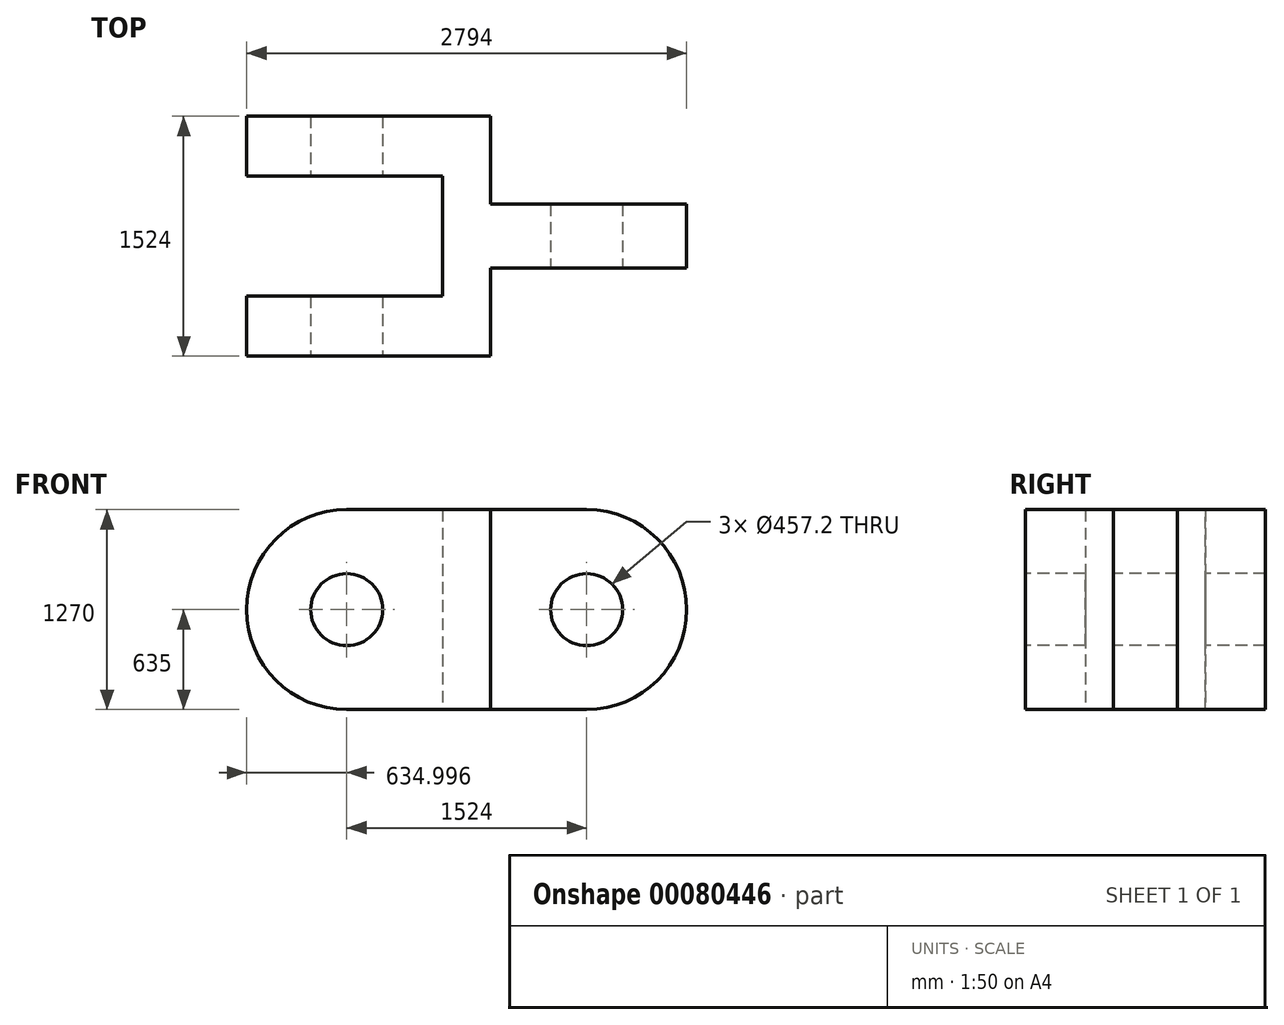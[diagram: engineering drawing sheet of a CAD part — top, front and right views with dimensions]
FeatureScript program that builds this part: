
annotation { "Feature Type Name" : "Feature", "Feature Type Description" : "" }
export const myFeature = defineFeature(function(context is Context, id is Id, definition is map)
    precondition{}
    {
        {
            var Q0;
            Q0=qCreatedBy(makeId("Top.planeOp"),FACE);
            var sketch = newSketch(context, id + "F0", { "sketchPlane" : qUnion([Q0])});
            skLineSegment(sketch, "E0", {"start": v(-848.91, 515.52) * mm, "end": v(-848.91, 134.52) * mm});
            skLineSegment(sketch, "E1", {"start": v(-848.91, 134.52) * mm, "end": v(395.69, 134.52) * mm});
            skLineSegment(sketch, "E2", {"start": v(395.69, 134.52) * mm, "end": v(395.69, -627.48) * mm});
            skLineSegment(sketch, "E3", {"start": v(395.69, -627.48) * mm, "end": v(-848.91, -627.48) * mm});
            skLineSegment(sketch, "E4", {"start": v(-848.91, -627.48) * mm, "end": v(-848.91, -1008.48) * mm});
            skLineSegment(sketch, "E5", {"start": v(-848.91, -1008.48) * mm, "end": v(700.49, -1008.48) * mm});
            skLineSegment(sketch, "E6", {"start": v(700.49, -1008.48) * mm, "end": v(700.49, -449.68) * mm});
            skLineSegment(sketch, "E7", {"start": v(700.49, -449.68) * mm, "end": v(1945.09, -449.68) * mm});
            skLineSegment(sketch, "E8", {"start": v(1945.09, -449.68) * mm, "end": v(1945.09, -43.28) * mm});
            skLineSegment(sketch, "E9", {"start": v(1945.09, -43.28) * mm, "end": v(700.49, -43.28) * mm});
            skLineSegment(sketch, "E10", {"start": v(700.49, -43.28) * mm, "end": v(700.49, 515.52) * mm});
            skLineSegment(sketch, "E11", {"start": v(700.49, 515.52) * mm, "end": v(-848.91, 515.52) * mm});
            skSolve(sketch);
        }
        {
            var Q0;
            Q0 = qSketchRegion(id + "F0", true);
            extrude(context, id + "F1", {"entities" : qUnion([Q0]), "depth" : 1270 * mm});
        }
        {
            var Q0;
            Q0=makeQuery(id+"F1.opExtrude","CAP_EDGE",EDGE,{"disambiguationData":[OSD([sQuery(id+"F0.wireOp",EDGE,"E8")])],"isStart":false});
            var Q1;
            Q1=makeQuery(id+"F1.opExtrude","CAP_EDGE",EDGE,{"disambiguationData":[OSD([sQuery(id+"F0.wireOp",EDGE,"E8")])],"isStart":true});
            var Q2;
            Q2=makeQuery(id+"F1.opExtrude","CAP_EDGE",EDGE,{"disambiguationData":[OSD([sQuery(id+"F0.wireOp",EDGE,"E4")])],"isStart":false});
            var Q3;
            Q3=makeQuery(id+"F1.opExtrude","CAP_EDGE",EDGE,{"disambiguationData":[OSD([sQuery(id+"F0.wireOp",EDGE,"E4")])],"isStart":true});
            var Q4;
            Q4=makeQuery(id+"F1.opExtrude","CAP_EDGE",EDGE,{"disambiguationData":[OSD([sQuery(id+"F0.wireOp",EDGE,"E0")])],"isStart":true});
            var Q5;
            Q5=makeQuery(id+"F1.opExtrude","CAP_EDGE",EDGE,{"disambiguationData":[OSD([sQuery(id+"F0.wireOp",EDGE,"E0")])],"isStart":false});
            fillet(context, id + "F2", {"entities" : qUnion([Q0, Q1, Q2, Q3, Q4, Q5]), "radius" : 635 * mm, "tangentPropagation" : true, "allowEdgeOverflow" : false});
        }
        {
            var Q0;
            Q0=makeQuery(id+"F1.opExtrude","SWEPT_FACE",FACE,{"disambiguationData":[OSD([sQuery(id+"F0.wireOp",EDGE,"E5")])]});
            var sketch = newSketch(context, id + "F3", { "sketchPlane" : qUnion([Q0])});
            skCircle(sketch, "E12", {"center": v(-213.91, 635) * mm, "radius": 228.6 * mm});
            skCircle(sketch, "E13", {"center": v(1310.09, 635) * mm, "radius": 228.6 * mm});
            skSolve(sketch);
        }
        {
            var Q0;
            Q0 = qSketchRegion(id + "F3", true);
            extrude(context, id + "F4", {"entities" : qUnion([Q0]), "operationType" : NewBodyOperationType.REMOVE, "oppositeDirection" : true, "depth" : 2540 * mm});
        }
    });
